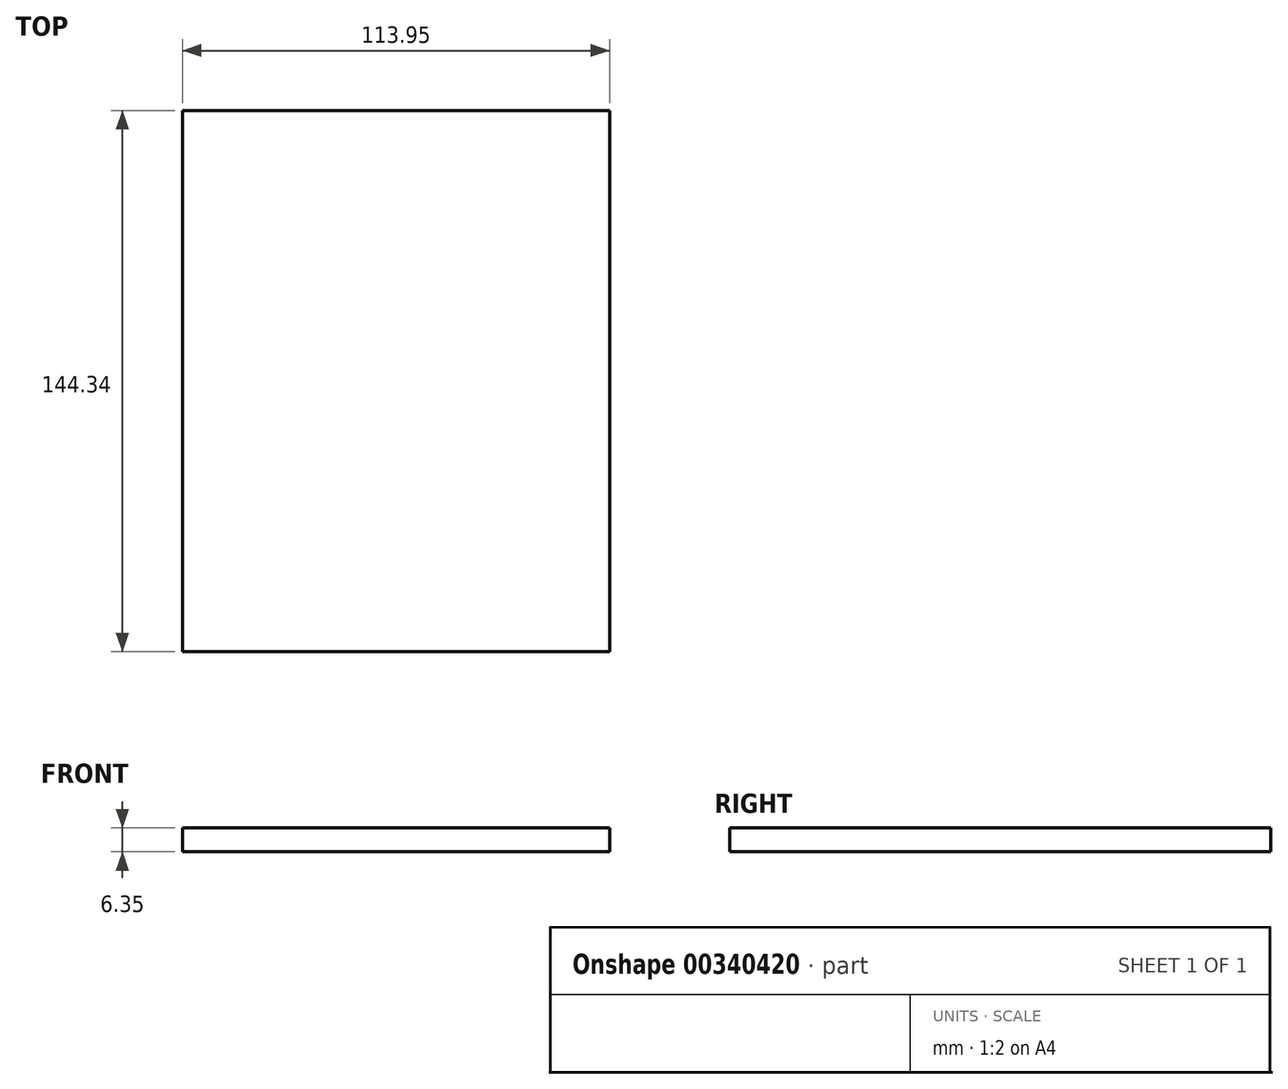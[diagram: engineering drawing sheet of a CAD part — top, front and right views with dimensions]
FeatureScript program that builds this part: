
annotation { "Feature Type Name" : "Feature", "Feature Type Description" : "" }
export const myFeature = defineFeature(function(context is Context, id is Id, definition is map)
    precondition{}
    {
        {
            var Q0;
            Q0=qCreatedBy(makeId("Top.planeOp"),FACE);
            var sketch = newSketch(context, id + "F0", { "sketchPlane" : qUnion([Q0])});
            skLineSegment(sketch, "E0.bottom", {"start": v(-55.66, 0) * mm, "end": v(58.29, 0) * mm});
            skLineSegment(sketch, "E0.top", {"start": v(-55.66, -144.34) * mm, "end": v(58.29, -144.34) * mm});
            skLineSegment(sketch, "E0.left", {"start": v(-55.66, 0) * mm, "end": v(-55.66, -144.34) * mm});
            skLineSegment(sketch, "E0.right", {"start": v(58.29, 0) * mm, "end": v(58.29, -144.34) * mm});
            skSolve(sketch);
        }
        {
            var Q0;
            Q0 = qSketchRegion(id + "F0", true);
            extrude(context, id + "F1", {"entities" : qUnion([Q0]), "depth" : 6.35 * mm, "offsetDistance" : 25.4 * mm});
        }
    });
